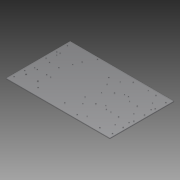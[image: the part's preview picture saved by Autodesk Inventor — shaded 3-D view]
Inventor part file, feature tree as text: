
AUTODESK INVENTOR PART (.ipt)
format: ipt  version: 2014 SP1 (Build 180222100, 222)  size: 206,848 bytes
history: native  units: in
note: dims shown in document units (in); Inventor stores cm internally (conversion verified against a paired STEP export)
features: reference x10, extrude x1, sketch x1
ambient origin geometry x8: Origin, YZ Plane, XZ Plane, XY Plane, X Axis, Y Axis, Z Axis, Center Point
bodies: Solid1 (feature_tree)
feature tree (12):
  extrude  "Extrusion1"  Depth=19.4375in
  sketch  "Sketch1"  dims[d0=12.0in d4=19.4375in d11=0.1875in d12=0.1875in d13=0.1875in d14=0.1875in d15=2.5in d17=8.25in d18=5.0in d20=4.5in d21=2.25in d30=0.125in d31=0.0in d32=0.5in d33=0.2in d34=1.0in d35=0.5in d37=1.0in d38=0.3937in d40=1.0in d41=2.3622in d43=2.0in d57=2.2032in d59=9.5in d67=6.5in d68=1.25in d69=2.29in d70=1.75in d71=1.0in d81=0.2in d85=0.375in d86=0.7874in d88=2.5in d89=0.7874in d91=4.5in d94=1.0in d96=0.1875in d97=0.1875in d98=0.1875in d99=0.1875in d100=1.25in d103=0.7605in d104=2.625in d105=0.7874in d107=4.25in d108=1.5748in d110=3.5in d113=1.646in d114=2.446in d115=0.15in d116=4.0in d117=0.2in d118=0.26in d119=0.2in d120=1.5in d121=0.2in d122=1.1811in d124=3.5in d125=0.3937in d127=1.0in d129=1.1811in d131=3.5in d132=0.3937in d134=1.0in]
  reference  "Reference1"
  reference  "Reference2"
  reference  "Reference3"
  reference  "Reference4"
  reference  "Reference5"
  reference  "Reference6"
  reference  "Reference7"
  reference  "Reference8"
  reference  "Reference9"
  reference  "Reference10"
